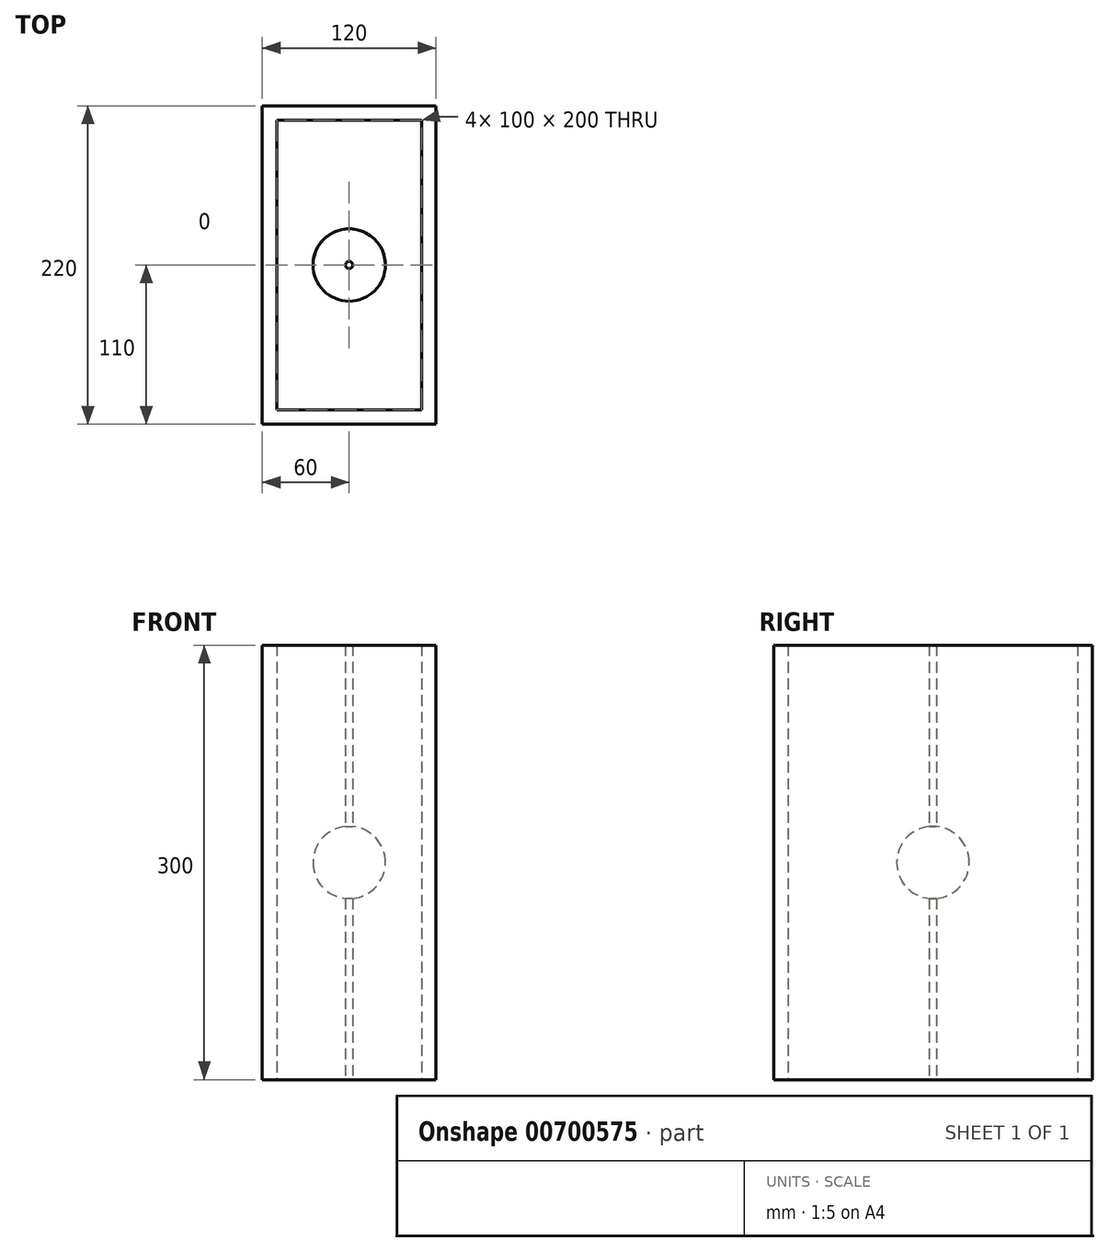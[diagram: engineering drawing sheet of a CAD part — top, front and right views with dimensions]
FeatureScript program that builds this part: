
annotation { "Feature Type Name" : "Feature", "Feature Type Description" : "" }
export const myFeature = defineFeature(function(context is Context, id is Id, definition is map)
    precondition{}
    {
        {
            var Q0;
            Q0=qCreatedBy(makeId("Top.planeOp"),FACE);
            var sketch = newSketch(context, id + "F0", { "sketchPlane" : qUnion([Q0])});
            skCircle(sketch, "E0", {"center": v(0, 0) * mm, "radius": 25 * mm});
            skCircle(sketch, "E1", {"center": v(0, 0) * mm, "radius": 2.5 * mm});
            skLineSegment(sketch, "E2", {"start": v(0, 0) * mm, "end": v(-67.7, 0) * mm});
            skLineSegment(sketch, "E3", {"start": v(0, 0) * mm, "end": v(109.23, 0) * mm});
            skLineSegment(sketch, "E4.bottom", {"start": v(-50, -100) * mm, "end": v(50, -100) * mm});
            skLineSegment(sketch, "E4.top", {"start": v(-50, 100) * mm, "end": v(50, 100) * mm});
            skLineSegment(sketch, "E4.left", {"start": v(-50, -100) * mm, "end": v(-50, 100) * mm});
            skLineSegment(sketch, "E4.right", {"start": v(50, -100) * mm, "end": v(50, 100) * mm});
            skLineSegment(sketch, "E5.0", {"start": v(-60, -110) * mm, "end": v(60, -110) * mm});
            skLineSegment(sketch, "E5.1", {"start": v(-60, -110) * mm, "end": v(-60, 110) * mm});
            skLineSegment(sketch, "E5.2", {"start": v(-60, 110) * mm, "end": v(60, 110) * mm});
            skLineSegment(sketch, "E5.3", {"start": v(60, -110) * mm, "end": v(60, 110) * mm});
            skSolve(sketch);
        }
        {
            var Q0;
            {var subQ0=sQuery(id+"F0.wireOp",EDGE,"E2");var subQ1=sQuery(id+"F0.wireOp",EDGE,"E1");var subQ2=makeQuery(id+"F0.imprint","INTERSECT",VERTEX,{"derivedFrom":[subQ1,subQ0]});Q0=makeQuery(id+"F0.imprint","IMPRINT",FACE,{"disambiguationData":[TD([[makeQuery(id+"F0.imprint","IMPRINT",EDGE,{"disambiguationData":[TD([[subQ2,-1.0]])],"derivedFrom":subQ1}),1.0]])]});}
            var Q1;
            {var subQ0=sQuery(id+"F0.wireOp",EDGE,"E2");var subQ1=sQuery(id+"F0.wireOp",EDGE,"E1");var subQ2=makeQuery(id+"F0.imprint","INTERSECT",VERTEX,{"derivedFrom":[subQ1,subQ0]});Q1=makeQuery(id+"F0.imprint","IMPRINT",FACE,{"disambiguationData":[TD([[makeQuery(id+"F0.imprint","IMPRINT",EDGE,{"disambiguationData":[TD([[subQ2,1.0]])],"derivedFrom":subQ1}),1.0]])]});}
            var Q2;
            {var subQ1=sQuery(id+"F0.wireOp",EDGE,"E4.top");Q2=makeQuery(id+"F0.imprint","IMPRINT",FACE,{"disambiguationData":[TD([[makeQuery(id+"F0.imprint","IMPRINT",EDGE,{"derivedFrom":subQ1}),1.0]])]});}
            var Q3;
            {var subQ1=sQuery(id+"F0.wireOp",EDGE,"E4.bottom");Q3=makeQuery(id+"F0.imprint","IMPRINT",FACE,{"disambiguationData":[TD([[makeQuery(id+"F0.imprint","IMPRINT",EDGE,{"derivedFrom":subQ1}),-1.0]])]});}
            extrude(context, id + "F1", {"entities" : qUnion([Q0, Q1, Q2, Q3]), "depth" : 150 * mm, "offsetDistance" : 25 * mm, "hasSecondDirection" : true, "secondDirectionOppositeDirection" : true, "secondDirectionDepth" : 150 * mm});
        }
        {
            var Q0;
            {var subQ0=sQuery(id+"F0.wireOp",EDGE,"E2");var subQ1=sQuery(id+"F0.wireOp",EDGE,"E0");var subQ2=makeQuery(id+"F0.imprint","INTERSECT",VERTEX,{"derivedFrom":[subQ1,subQ0]});Q0=makeQuery(id+"F0.imprint","IMPRINT",FACE,{"disambiguationData":[TD([[makeQuery(id+"F0.imprint","IMPRINT",EDGE,{"disambiguationData":[TD([[subQ2,-1.0]])],"derivedFrom":subQ1}),1.0]])]});}
            var Q1;
            Q1=sQuery(id+"F0.wireOp",EDGE,"E2");
            revolve(context, id + "F2", {"operationType" : NewBodyOperationType.ADD, "entities" : qUnion([Q0]), "axis" : qUnion([Q1]), "revolveType" : RevolveType.FULL});
        }
    });
